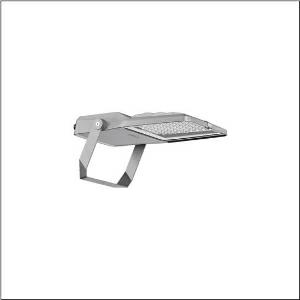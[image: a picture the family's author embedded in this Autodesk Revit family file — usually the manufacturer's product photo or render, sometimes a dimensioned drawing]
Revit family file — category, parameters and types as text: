
# Revit family: floodlight_fl_21_mini___rs12_5xa7772b1b1a_a118
name_source: partatom
category: Lighting Fixtures
units: mm (PartAtom-declared; Revit-internal decimal feet)

## family parameters
Cut with Voids When Loaded = No
Host = Face
Light Source = No
Part Type = Normal
Room Calculation Point = No
Round Connector Dimension = Use Diameter
Shared = No

## types (1)
- --- (1 x LED, 5230 lm, 45.5 W, 2200K)
    Apparent Load = 46 VA
    CIE Flux Codes = 79 92 99 100 100
    Color Rendering = 70
    Color Temperature = 2200K
    Default Elevation = 1800 mm
    Description = Floodlight FL 21 mini, floodlight, primary light control with lens, of PMMA, primary optical cover: protective disc, of toughened safety glass, transparent, light distribution: RS12, light emission: direct distribution, installation type: surface-mounted, LED, High Power LED, rated luminous flux: 5.230lm, luminous efficacy: 115lm/W, light colour: 722, colour temperature: 2200K, control gear: ECG iQ, control: Street-Remote, Auto-Match, Temp-Guard, Night-Set, Smart-Wire, Desk-Remote (wireless, voltage-free reading and setting of iQ features in the workshop via application-optimized NFC function/RFID function), optimised constant luminous flux control (CLO 2.0), with terminal, 6-pole, mains connection: 220..240V, AC, 50/60Hz, start of lifetime: 46W, end of lifetime: 48W, reduction: 21W, luminaire housing, of diecast aluminium, powder-coated, Siteco® metallic grey (DB 702S), corrosivity category C5 according to DIN EN ISO 12944, mounting bracket, of steel, galvanised, powder-coated, Siteco® metallic grey (DB 702S), protection rating (complete): IP66, insulation class (complete): insulation class II (safety insulation), certification: CE, ENEC, VDE, protection symbol: D, impact resistance: IK08, permissible operating ambient temperature: -40..+40°C, permissible operating ambient temperature for outdoor applications: -40..+50°C, standard: DIN EN 12944, packaging unit: 1 piece

Light Distribution: RS12
    Height = 70 mm
    Lamp = 1 x LED
    Lamp Light Flux = 5230 lm
    Lamp Power = 45.5 W
    Lamp count = 1
    Length = 485 mm
    Luminous efficacy = 115 lm/W
    Manufacturer = Siteco
    ModVariant = No
    Model = 5XA7772B1B1A
    Number of Poles = 1
    OnlyDefault = Yes
    Power Factor = 1
    Product Name = Floodlight FL 21 mini | RS12
    Product group = floodlight | pylon top
    ProductGroupID = 6101
    Protection Class = Protection class II
    Protection Degree = IP 66
    RLX_Detail_Level = 1
    RlxData = <blob elided: 90609 chars, md5=341b6e1e>
    Socket = socket
    Standby Power = 0 W
    System Light Flux = 5230 lm
    System Power = 46 W
    Type Comments = factory setting: luminous flux: 100 % | dim-lin: 254 | 463 mA
    Type Image = l_1006845.jpg
    URL = http://relux.com
    VarID = @adj_078991
    Voltage = 0 V
    Weight = 0.00 kg
    Width = 337 mm

## geometry (parser evidence)
native form markers: Blend x4, Sweep x12
no freeform markers — native parametric forms only
